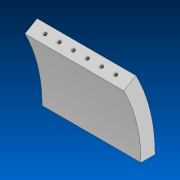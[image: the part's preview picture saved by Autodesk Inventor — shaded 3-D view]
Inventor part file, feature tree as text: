
AUTODESK INVENTOR PART (.ipt)
format: ipt  version: 2022.2 (Build 262287000, 287)  size: 134,656 bytes
history: native  units: in
note: dims shown in document units (in); Inventor stores cm internally (conversion verified against a paired STEP export)
features: sketch x3, hole x2, pattern_linear x2, extrude x1
ambient origin geometry x8: Origin, YZ Plane, XZ Plane, XY Plane, X Axis, Y Axis, Z Axis, Center Point
bodies: Solid1 (feature_tree)
feature tree (8):
  extrude  "Extrusion1"  TaperAngle=30.0deg  [1 undecoded]
  hole  "Hole1"  [1 undecoded]
  hole  "Hole2"  [1 undecoded]
  pattern_linear  "Rectangular Pattern1"  Spacing1=0.5in  [1 undecoded]
  pattern_linear  "Rectangular Pattern2"  Spacing1=1.0in  [1 undecoded]
  sketch  "Sketch1"  dims[d1=10.9074in d2=30.0deg]
  sketch  "Sketch2"  dims[d4=1.0in d5=1.0in]
  sketch  "Sketch3"  dims[d6=7.0in d7=0.0in d8=0.5in d9=0.5in d10=0.175in d11=0.75in d12=0.22in d13=0.325in d14=0.5635in d15=1.5in d16=0.0in d17=1.0in d18=0.5in d19=0.175in d20=0.75in d21=0.22in d22=0.325in d23=0.5635in d24=1.5in d25=0.0in d26=2.7559in d28=1.0in d29=2.3622in d31=1.0in]
note: 5 required parameter values undecoded (feature->parameter linkage not recoverable at this tier; creation-order binding heuristic only, values carry confidence <= 0.55)
